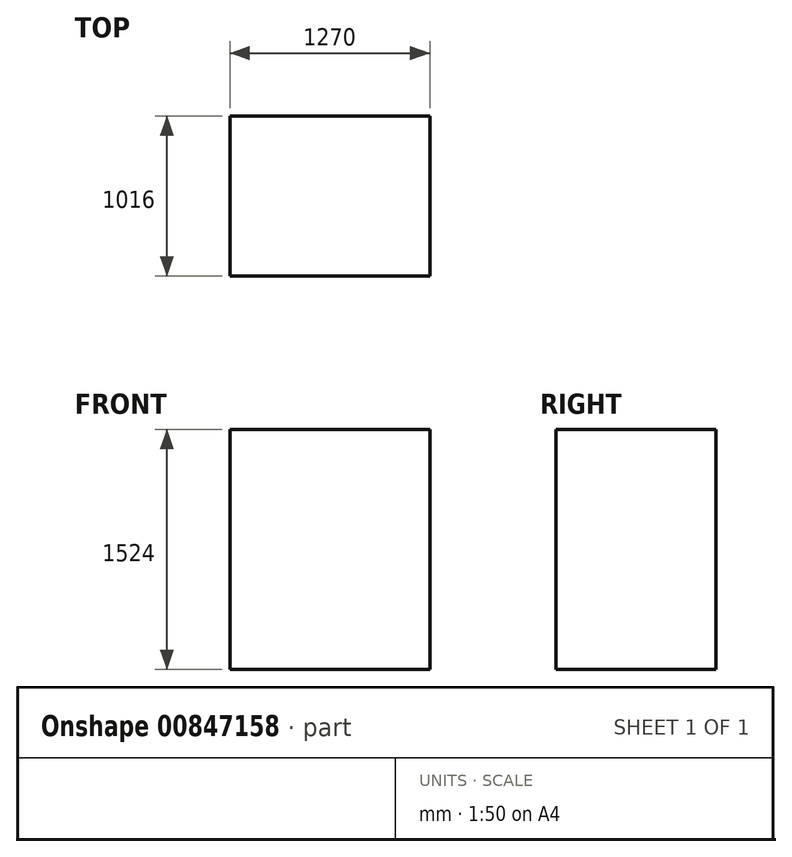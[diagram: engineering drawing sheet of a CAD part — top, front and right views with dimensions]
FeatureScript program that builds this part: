
annotation { "Feature Type Name" : "Feature", "Feature Type Description" : "" }
export const myFeature = defineFeature(function(context is Context, id is Id, definition is map)
    precondition{}
    {
        {
            var Q0;
            Q0=qCreatedBy(makeId("Top.planeOp"),FACE);
            var sketch = newSketch(context, id + "F0", { "sketchPlane" : qUnion([Q0])});
            skLineSegment(sketch, "E0.bottom", {"start": v(-635, 508) * mm, "end": v(635, 508) * mm});
            skLineSegment(sketch, "E0.top", {"start": v(-635, -508) * mm, "end": v(635, -508) * mm});
            skLineSegment(sketch, "E0.left", {"start": v(-635, 508) * mm, "end": v(-635, -508) * mm});
            skLineSegment(sketch, "E0.right", {"start": v(635, 508) * mm, "end": v(635, -508) * mm});
            skPoint(sketch, "E0.middle", {"position": v(0, 0) * mm});
            skSolve(sketch);
        }
        {
            var Q0;
            Q0=makeQuery(id+"F0.imprint","IMPRINT",FACE,{"disambiguationData":[TD([[makeQuery(id+"F0.imprint","IMPRINT",EDGE,{"derivedFrom":sQuery(id+"F0.wireOp",EDGE,"E0.bottom")}),-1.0]])]});
            extrude(context, id + "F1", {"entities" : qUnion([Q0]), "depth" : 1524 * mm, "offsetDistance" : 25.4 * mm});
        }
    });
